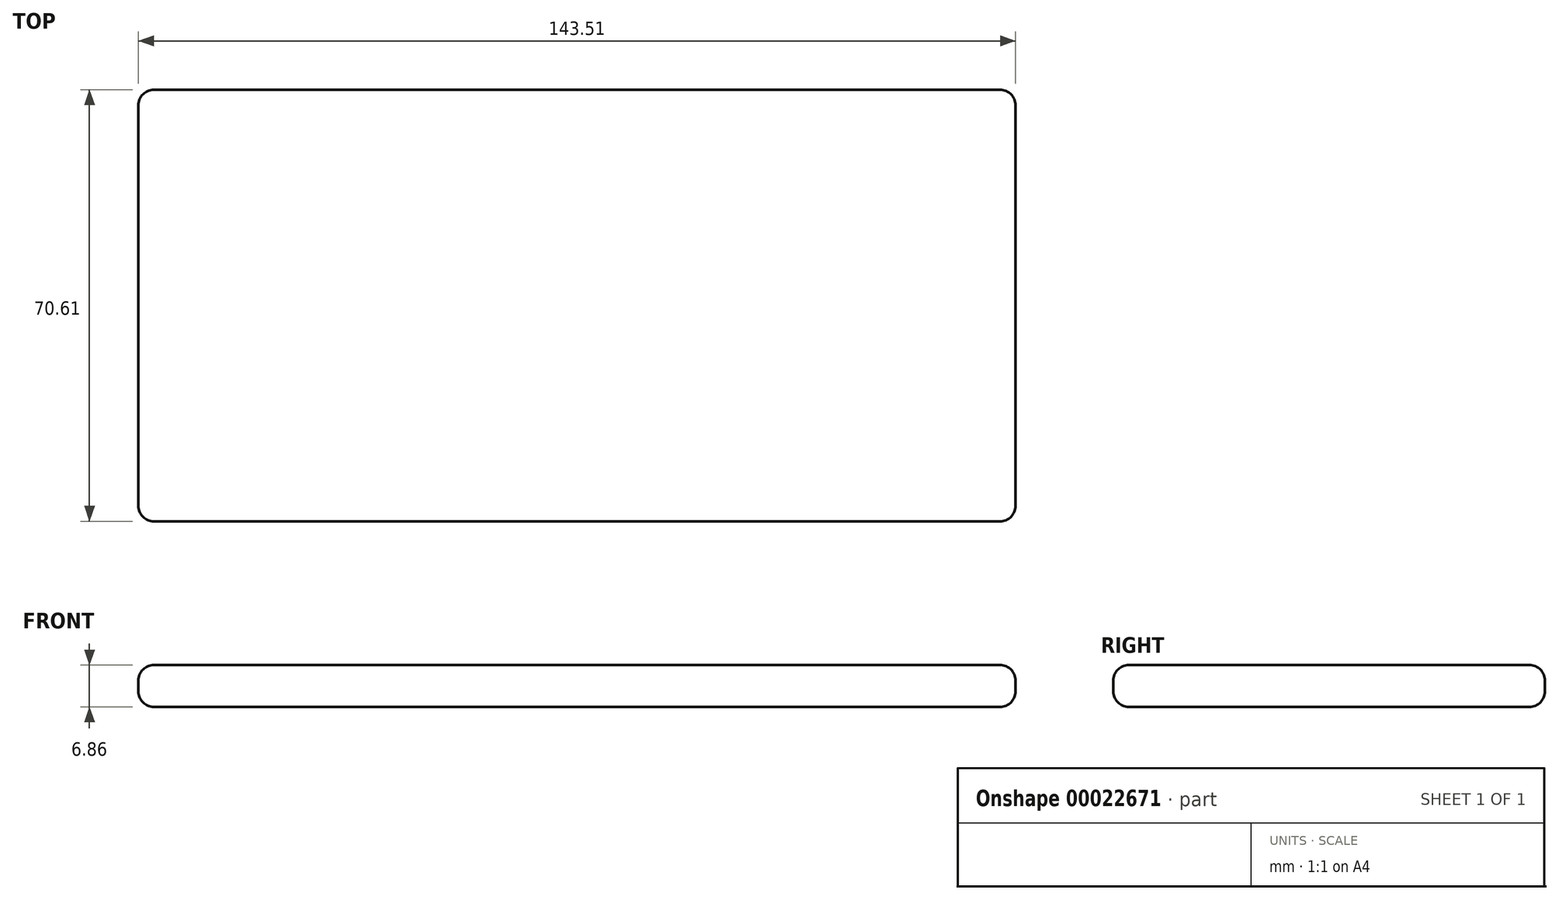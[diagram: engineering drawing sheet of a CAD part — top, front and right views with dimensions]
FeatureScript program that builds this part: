
annotation { "Feature Type Name" : "Feature", "Feature Type Description" : "" }
export const myFeature = defineFeature(function(context is Context, id is Id, definition is map)
    precondition{}
    {
        {
            var Q0;
            Q0=qCreatedBy(makeId("Top.planeOp"),FACE);
            var sketch = newSketch(context, id + "F0", { "sketchPlane" : qUnion([Q0])});
            skLineSegment(sketch, "E0.bottom", {"start": v(-73.46, -24.77) * mm, "end": v(70.05, -24.77) * mm});
            skLineSegment(sketch, "E0.top", {"start": v(-73.46, 45.84) * mm, "end": v(70.05, 45.84) * mm});
            skLineSegment(sketch, "E0.left", {"start": v(-73.46, -24.77) * mm, "end": v(-73.46, 45.84) * mm});
            skLineSegment(sketch, "E0.right", {"start": v(70.05, -24.77) * mm, "end": v(70.05, 45.84) * mm});
            skSolve(sketch);
        }
        {
            var Q0;
            Q0=makeQuery(id+"F0.imprint","IMPRINT",FACE,{"disambiguationData":[TD([[makeQuery(id+"F0.imprint","IMPRINT",EDGE,{"derivedFrom":sQuery(id+"F0.wireOp",EDGE,"E0.bottom")}),1.0]])]});
            extrude(context, id + "F1", {"entities" : qUnion([Q0]), "depth" : 6.86 * mm});
        }
        {
            var Q0;
            Q0=makeQuery(id+"F1.opExtrude","CAP_EDGE",EDGE,{"disambiguationData":[OSD([sQuery(id+"F0.wireOp",EDGE,"E0.left")])],"isStart":false});
            var Q1;
            Q1=makeQuery(id+"F1.opExtrude","CAP_EDGE",EDGE,{"disambiguationData":[OSD([sQuery(id+"F0.wireOp",EDGE,"E0.bottom")])],"isStart":false});
            var Q2;
            Q2=makeQuery(id+"F1.opExtrude","CAP_EDGE",EDGE,{"disambiguationData":[OSD([sQuery(id+"F0.wireOp",EDGE,"E0.top")])],"isStart":false});
            var Q3;
            Q3=makeQuery(id+"F1.opExtrude","CAP_EDGE",EDGE,{"disambiguationData":[OSD([sQuery(id+"F0.wireOp",EDGE,"E0.right")])],"isStart":false});
            var Q4;
            Q4=makeQuery(id+"F1.opExtrude","CAP_EDGE",EDGE,{"disambiguationData":[OSD([sQuery(id+"F0.wireOp",EDGE,"E0.right")])],"isStart":true});
            var Q5;
            Q5=makeQuery(id+"F1.opExtrude","CAP_EDGE",EDGE,{"disambiguationData":[OSD([sQuery(id+"F0.wireOp",EDGE,"E0.bottom")])],"isStart":true});
            var Q6;
            Q6=makeQuery(id+"F1.opExtrude","CAP_EDGE",EDGE,{"disambiguationData":[OSD([sQuery(id+"F0.wireOp",EDGE,"E0.left")])],"isStart":true});
            var Q7;
            Q7=makeQuery(id+"F1.opExtrude","CAP_EDGE",EDGE,{"disambiguationData":[OSD([sQuery(id+"F0.wireOp",EDGE,"E0.top")])],"isStart":true});
            var Q8;
            Q8=makeQuery(id+"F1.opExtrude","SWEPT_EDGE",EDGE,{"disambiguationData":[OSD([sQuery(id+"F0.wireOp",EDGE,"E0.bottom"),sQuery(id+"F0.wireOp",EDGE,"E0.right")])]});
            var Q9;
            Q9=makeQuery(id+"F1.opExtrude","SWEPT_EDGE",EDGE,{"disambiguationData":[OSD([sQuery(id+"F0.wireOp",EDGE,"E0.top"),sQuery(id+"F0.wireOp",EDGE,"E0.right")])]});
            var Q10;
            Q10=makeQuery(id+"F1.opExtrude","SWEPT_EDGE",EDGE,{"disambiguationData":[OSD([sQuery(id+"F0.wireOp",EDGE,"E0.bottom"),sQuery(id+"F0.wireOp",EDGE,"E0.left")])]});
            var Q11;
            Q11=makeQuery(id+"F1.opExtrude","SWEPT_EDGE",EDGE,{"disambiguationData":[OSD([sQuery(id+"F0.wireOp",EDGE,"E0.top"),sQuery(id+"F0.wireOp",EDGE,"E0.left")])]});
            fillet(context, id + "F2", {"entities" : qUnion([Q0, Q1, Q2, Q3, Q4, Q5, Q6, Q7, Q8, Q9, Q10, Q11]), "radius" : 2.54 * mm, "tangentPropagation" : true, "allowEdgeOverflow" : false});
        }
    });
